FCSTD DOCUMENT  (FreeCAD 0.16R)
Label: chainguard30tV5
License: All rights reserved
LicenseURL: http://en.wikipedia.org/wiki/All_rights_reserved
objects: Sketcher::SketchObject×10, PartDesign::Pocket×6, PartDesign::Fillet×5, PartDesign::Pad×4, Part::FeaturePython×3, Mesh::Feature×3
note: 38 computed .brp shape members not serialized (recipe doc carries the construction recipe); baked Part::Feature solids carry a one-line shape summary decoded from their .brp

FEATURE [Sketcher::SketchObject] Sketch001
  sketch-geometry (8):
    g0: LineSegment StartX=73 StartY=74 StartZ=0 EndX=0 EndY=74 EndZ=0
    g1: ArcOfCircle CenterX=0 CenterY=0 CenterZ=0 NormalX=0 NormalY=0 NormalZ=1 Radius=74 StartAngle=1.5708 EndAngle=3.14159
    g2: LineSegment StartX=73 StartY=74 StartZ=0 EndX=73 EndY=52.8786 EndZ=0
    g3: ArcOfCircle CenterX=50.1336 CenterY=52.8786 CenterZ=0 NormalX=0 NormalY=0 NormalZ=1 Radius=22.8664 StartAngle=3.95363 EndAngle=6.28319
    g4: LineSegment StartX=-71 StartY=-3 StartZ=0 EndX=-63 EndY=-3 EndZ=0
    g5: ArcOfCircle CenterX=-63 CenterY=10.9434 CenterZ=0 NormalX=0 NormalY=0 NormalZ=1 Radius=13.9434 StartAngle=4.71239 EndAngle=6.1112
    g6: ArcOfCircle CenterX=-71 CenterY=1.3209e-07 CenterZ=0 NormalX=0 NormalY=0 NormalZ=1 Radius=3 StartAngle=3.14159 EndAngle=4.71239
    g7: ArcOfCircle CenterX=0 CenterY=0 CenterZ=0 NormalX=0 NormalY=0 NormalZ=1 Radius=50 StartAngle=0.81204 EndAngle=2.9696
  constraints (29):
    c: Horizontal(g0)
    c: Coincident(g0,g1)
    c: DistanceX(g0,g0) = 73
    c: Vertical(g2)
    c: DistanceX(g-1,g2) = 73
    c: Radius(g1) = 74
    c: Tangent(g2,g3) = 1.5708
    c: DistanceY(g-1,g0) = 74
    c: DistanceX(g-1,g0) = 0
    c: Horizontal(g4)
    c: DistanceX(g1,g-1) = 74
    c: Coincident(g5,g4)
    c: PointOnObject(g1,g-1)
    c: PointOnObject(g6,g-1)
    c: Coincident(g6,g1)
    c: Coincident(g4,g6)
    c: Tangent(g6,g1)
    c: Tangent(g4,g6)
    c: Tangent(g5,g4)
    c: Coincident(g7,g-1)
    c: Radius(g7) = 50
    c: DistanceX(g4,g4) = 8
    c: DistanceY(g4) = -3
    c: Coincident(g7,g5)
    c: Tangent(g5,g7)
    c: Coincident(g7,g3)
    c: Tangent(g3,g7)
    c: DistanceY(g5) = 8.5571
    c: DistanceY(g3) = 36.2846
FEATURE [PartDesign::Pad] Pad  label="Faceplate"
  Length = 1
  Length2 = 100
  Reversed = true
  Sketch = -> Sketch001
  Type = 0
FEATURE [Sketcher::SketchObject] Sketch002
  sketch-geometry (6):
    g0: LineSegment StartX=73 StartY=74 StartZ=0 EndX=0 EndY=74 EndZ=0
    g1: ArcOfCircle CenterX=3.08522e-07 CenterY=0 CenterZ=0 NormalX=0 NormalY=0 NormalZ=1 Radius=74 StartAngle=1.5708 EndAngle=3.14159
    g2: LineSegment StartX=0 StartY=72 StartZ=0 EndX=73 EndY=72 EndZ=0
    g3: LineSegment StartX=73 StartY=74 StartZ=0 EndX=73 EndY=72 EndZ=0
    g4: ArcOfCircle CenterX=6.89957e-06 CenterY=0 CenterZ=0 NormalX=0 NormalY=0 NormalZ=1 Radius=72 StartAngle=1.5708 EndAngle=3.14159
    g5: ArcOfCircle CenterX=-73 CenterY=0 CenterZ=0 NormalX=0 NormalY=0 NormalZ=1 Radius=1 StartAngle=3.14159 EndAngle=6.28319
  constraints (21):
    c: Horizontal(g0)
    c: Coincident(g0,g1)
    c: Parallel(g0,g2)
    c: DistanceY(g2,g0) = 2
    c: DistanceX(g0) = 73
    c: Equal(g2,g0)
    c: Coincident(g3,g2)
    c: Coincident(g3,g0)
    c: Coincident(g4,g2)
    c: Radius(g4) = 72
    c: Radius(g1) = 74
    c: DistanceY(g-1,g0) = 74
    c: DistanceX(g2) = 0
    c: DistanceX(g0) = 0
    c: Tangent(g1,g0)
    c: Tangent(g4,g2)
    c: PointOnObject(g5,g-1)
    c: Coincident(g5,g4)
    c: Coincident(g5,g1)
    c: PointOnObject(g5,g-1)
    c: PointOnObject(g4,g-1)
FEATURE [PartDesign::Pad] Pad001  label="Connector"
  Length = 12
  Length2 = 100
  Sketch = -> Sketch002
  Type = 0
FEATURE [Sketcher::SketchObject] Sketch
  Support = -> Pad [Face9]
  sketch-geometry (5):
    g0: LineSegment [constr] StartX=1.2 StartY=2 StartZ=0 EndX=58.5173 EndY=86.9764 EndZ=0
    g1: LineSegment StartX=27.4353 StartY=72.1905 StartZ=0 EndX=73.0254 EndY=72.1905 EndZ=0
    g2: LineSegment StartX=73.0254 StartY=77.1905 StartZ=0 EndX=44.0091 EndY=96.7622 EndZ=0
    g3: LineSegment StartX=44.0091 StartY=96.7622 StartZ=0 EndX=27.4353 EndY=72.1905 EndZ=0
    g4: LineSegment StartX=73.0254 StartY=77.1905 StartZ=0 EndX=73.0254 EndY=72.1905 EndZ=0
  constraints (15):
    c: DistanceY(g-1,g0) = 2
    c: DistanceX(g0,g-1) = -1.2
    c: Angle(g0) = 0.977384
    c: Distance(g0) = 102.5
    c: Horizontal(g1)
    c: Coincident(g2,g3)
    c: Coincident(g1,g3)
    c: Parallel(g0,g3)
    c: Symmetric(g2,g2,g0)
    c: Distance(g2) = 35
    c: PointOnObject(g0,g2)
    c: Coincident(g4,g2)
    c: Coincident(g4,g1)
    c: Vertical(g4)
    c: DistanceY(g4,g4) = 5
FEATURE [Sketcher::SketchObject] Sketch025
  sketch-geometry (5):
    g0: LineSegment [constr] StartX=-4 StartY=2 StartZ=0 EndX=-74.2884 EndY=23.4893 EndZ=0
    g1: LineSegment StartX=-69.1719 StartY=40.2247 StartZ=0 EndX=-79.4049 EndY=6.75399 EndZ=0
    g2: LineSegment StartX=-79.4049 StartY=6.75399 StartZ=0 EndX=-73.6671 EndY=4.99976 EndZ=0
    g3: LineSegment StartX=-73.6671 StartY=4.99976 StartZ=0 EndX=-63.4341 EndY=38.4704 EndZ=0
    g4: LineSegment StartX=-63.4341 StartY=38.4704 StartZ=0 EndX=-69.1719 EndY=40.2247 EndZ=0
  constraints (16):
    c: DistanceY(g-1,g0) = 2
    c: DistanceX(g0,g-1) = 4
    c: Angle(g0) = 2.84489
    c: Coincident(g1,g2)
    c: Coincident(g2,g3)
    c: Coincident(g3,g4)
    c: Coincident(g4,g1)
    c: Distance(g4) = 6
    c: Parallel(g2,g0)
    c: Parallel(g0,g4)
    c: Equal(g4,g2)
    c: Perpendicular(g0,g1)
    c: PointOnObject(g0,g1)
    c: Symmetric(g1,g1,g0)
    c: Distance(g0) = 73.5
    c: Distance(g1) = 35
FEATURE [PartDesign::Pad] Pad004  label="SyncBoss"
  Length = 32
  Length2 = 1
  Sketch = -> Sketch025
  Type = 4
FEATURE [Sketcher::SketchObject] Sketch027
  Placement = pos=(-74.5057,22.7787,0) rot=(-0.463605,0.626526,0.626526;4.00981rad)
  Support = -> Pad004 [Face23]
  sketch-geometry (1):
    g0: Circle CenterX=-0.743123 CenterY=31 CenterZ=0 NormalX=0 NormalY=0 NormalZ=1 Radius=11.2
FEATURE [PartDesign::Pocket] Pocket001  label="SyncHole"
  Length = 5
  Sketch = -> Sketch027
  Type = 1
FEATURE [Sketcher::SketchObject] Sketch033
  ExternalGeometry = -> [Pocket001]
  Placement = pos=(0,0,32) rot=(0,0,1;0rad)
  Support = -> Pocket001 [Face7]
  sketch-geometry (2):
    g0: Circle CenterX=-67.3394 CenterY=35.9577 CenterZ=0 NormalX=0 NormalY=0 NormalZ=1 Radius=1.4
    g1: Circle CenterX=-75.5258 CenterY=9.18116 CenterZ=0 NormalX=0 NormalY=0 NormalZ=1 Radius=1.4
  constraints (6):
    c: Equal(g1,g0)
    c: Radius(g0) = 1.4
    c: Distance(g0,g-4) = 3
    c: Distance(g1,g-7) = 3
    c: Distance(g1,g0) = 28
    c: Distance(g0,g-3) = 2.8
FEATURE [PartDesign::Pocket] Pocket005  label="SyncHoles"
  Length = 15
  Sketch = -> Sketch033
  Type = 0
FEATURE [PartDesign::Fillet] Fillet001
  Base = -> Pocket005 [Edge1]
  Radius = 4
FEATURE [PartDesign::Fillet] Fillet002
  Base = -> Fillet001 [Edge4,Edge12,Edge17,Edge18,Edge19,Edge1,Edge8,Edge9,Edge10,Edge11]
  Radius = 1
FEATURE [PartDesign::Pad] Pad005
  Length = 32
  Length2 = 1
  Sketch = -> Sketch
  Type = 4
FEATURE [Sketcher::SketchObject] Sketch036
  ExternalGeometry = -> [Pad005]
  Placement = pos=(73.0254,0,0) rot=(0.57735,0.57735,0.57735;2.0944rad)
  Support = -> Pad005 [Face15]
  sketch-geometry (3):
    g0: ArcOfCircle CenterX=72.1905 CenterY=23.5718 CenterZ=0 NormalX=0 NormalY=0 NormalZ=1 Radius=24.5718 StartAngle=4.71239 EndAngle=6.28319
    g1: LineSegment StartX=96.7622 StartY=23.5718 StartZ=0 EndX=109.953 EndY=-14.1906 EndZ=0
    g2: LineSegment StartX=72.1905 StartY=-1 StartZ=0 EndX=109.953 EndY=-14.1906 EndZ=0
  constraints (9):
    c: Coincident(g0,g-6)
    c: PointOnObject(g0,g-3)
    c: Tangent(g0,g-3)
    c: Tangent(g0,g-6)
    c: Coincident(g1,g2)
    c: Coincident(g1,g0)
    c: Coincident(g2,g0)
    c: Equal(g1,g2)
    c: Distance(g1) = 40
FEATURE [PartDesign::Pocket] Pocket  label="STOuterRadius"
  Length = 5
  Sketch = -> Sketch036
  Type = 1
FEATURE [Sketcher::SketchObject] Sketch031
  ExternalGeometry = -> [Pocket]
  Placement = pos=(-14.6106,9.85496,0) rot=(-0.351924,0.661872,0.661872;3.81837rad)
  Support = -> Pocket [Face12]
  sketch-geometry (3):
    g0: ArcOfCircle CenterX=-78.549 CenterY=32 CenterZ=0 NormalX=0 NormalY=0 NormalZ=1 Radius=20.2801 StartAngle=3.14159 EndAngle=4.87878
    g1: LineSegment StartX=-98.8291 StartY=32 StartZ=0 EndX=-63.1873 EndY=50.1567 EndZ=0
    g2: LineSegment StartX=-63.1873 StartY=50.1567 StartZ=0 EndX=-75.1902 EndY=12 EndZ=0
  constraints (10):
    c: Coincident(g0,g1)
    c: Coincident(g0,g2)
    c: Coincident(g1,g2)
    c: PointOnObject(g0,g-3)
    c: PointOnObject(g0,g-4)
    c: DistanceX(g-3,g0) = 6
    c: DistanceY(g-4,g0) = 12
    c: Distance(g1) = 40
    c: Equal(g2,g1)
    c: Perpendicular(g0,g-3)
FEATURE [PartDesign::Pocket] Pocket006  label="STInnerRadius"
  Length = 5
  Sketch = -> Sketch031
  Type = 1
FEATURE [Sketcher::SketchObject] Sketch029
  ExternalGeometry = -> [Pocket006]
  Placement = pos=(58.6197,86.9073,0) rot=(0.211303,0.691141,0.691141;2.72511rad)
  Support = -> Pocket006 [Face17]
  sketch-geometry (1):
    g0: Circle CenterX=0.123541 CenterY=32 CenterZ=0 NormalX=0 NormalY=0 NormalZ=1 Radius=11.2
  constraints (2):
    c: Radius(g0) = 11.2
    c: Symmetric(g-3,g-3,g0)
FEATURE [PartDesign::Pocket] Pocket007  label="STHole"
  Length = 5
  Sketch = -> Sketch029
  Type = 1
FEATURE [Sketcher::SketchObject] Sketch034
  ExternalGeometry = -> [Pocket007]
  Placement = pos=(0,0,32) rot=(0,0,1;0rad)
  Support = -> Pocket007 [Face17]
  sketch-geometry (2):
    g0: Circle CenterX=45.2332 CenterY=92.3179 CenterZ=0 NormalX=0 NormalY=0 NormalZ=1 Radius=1.4
    g1: Circle CenterX=68.4462 CenterY=76.6605 CenterZ=0 NormalX=0 NormalY=0 NormalZ=1 Radius=1.4
  constraints (6):
    c: Equal(g1,g0)
    c: Radius(g0) = 1.4
    c: Distance(g0,g-3) = 2.8
    c: Distance(g1,g-4) = 2.8
    c: Distance(g1,g-5) = 3
    c: Distance(g0,g-8) = 3
FEATURE [PartDesign::Pocket] Pocket008  label="STScrewHoles"
  Length = 15
  Sketch = -> Sketch034
  Type = 0
FEATURE [PartDesign::Fillet] Fillet
  Base = -> Pocket008 [Edge36]
  Radius = 2
FEATURE [PartDesign::Fillet] Fillet003
  Base = -> Fillet [Edge25]
  Radius = 2
FEATURE [PartDesign::Fillet] Fillet004
  Base = -> Fillet003 [Edge22]
  Radius = 1
FEATURE [Part::FeaturePython] refine  label="refine_Fillet"  # WARN: FeaturePython — macro-defined, semantics opaque (R4)
  Base = -> Fillet
FEATURE [Part::FeaturePython] refine001  label="refine_Connector"  # WARN: FeaturePython — macro-defined, semantics opaque (R4)
  Base = -> Pad001
FEATURE [Part::FeaturePython] refine002  label="refine_Fillet002"  # WARN: FeaturePython — macro-defined, semantics opaque (R4)
  Base = -> Fillet002
FEATURE [Mesh::Feature] Mesh  label="refine_Fillet (Meshed)"
FEATURE [Mesh::Feature] Mesh001  label="refine_Connector (Meshed)"
FEATURE [Mesh::Feature] Mesh002  label="refine_Fillet002 (Meshed)"
